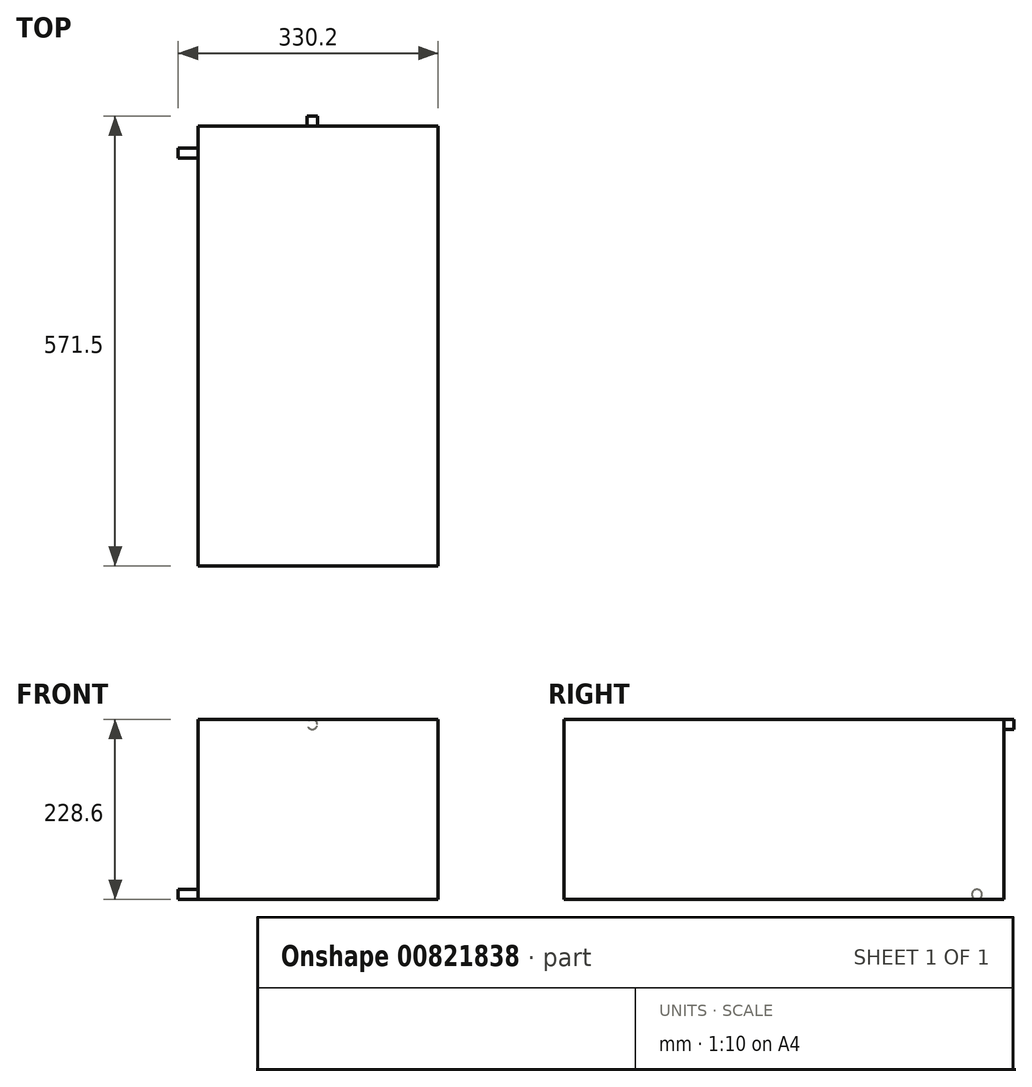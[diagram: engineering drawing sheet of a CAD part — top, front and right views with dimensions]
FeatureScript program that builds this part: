
annotation { "Feature Type Name" : "Feature", "Feature Type Description" : "" }
export const myFeature = defineFeature(function(context is Context, id is Id, definition is map)
    precondition{}
    {
        {
            var Q0;
            Q0=qCreatedBy(makeId("Top.planeOp"),FACE);
            var sketch = newSketch(context, id + "F0", { "sketchPlane" : qUnion([Q0])});
            skLineSegment(sketch, "E0", {"start": v(0, 0) * mm, "end": v(-304.8, 0) * mm});
            skLineSegment(sketch, "E1", {"start": v(0, 0) * mm, "end": v(0, 558.8) * mm});
            skLineSegment(sketch, "E2", {"start": v(0, 558.8) * mm, "end": v(-304.8, 558.8) * mm});
            skLineSegment(sketch, "E3", {"start": v(-304.8, 558.8) * mm, "end": v(-304.8, 0) * mm});
            skSolve(sketch);
        }
        {
            var Q0;
            Q0 = qSketchRegion(id + "F0", true);
            extrude(context, id + "F1", {"entities" : qUnion([Q0]), "depth" : 228.6 * mm, "offsetDistance" : 25.4 * mm});
        }
        {
            var Q0;
            Q0=makeQuery(id+"F1.opExtrude","SWEPT_FACE",FACE,{"disambiguationData":[OSD([sQuery(id+"F0.wireOp",EDGE,"E3")])]});
            var sketch = newSketch(context, id + "F2", { "sketchPlane" : qUnion([Q0])});
            skCircle(sketch, "E4", {"center": v(-524.49, 6.35) * mm, "radius": 6.35 * mm});
            skSolve(sketch);
        }
        {
            var Q0;
            Q0 = qSketchRegion(id + "F2", true);
            extrude(context, id + "F3", {"entities" : qUnion([Q0]), "operationType" : NewBodyOperationType.ADD, "depth" : 25.4 * mm, "offsetDistance" : 25.4 * mm});
        }
        {
            var Q0;
            Q0=makeQuery(id+"F1.opExtrude","SWEPT_FACE",FACE,{"disambiguationData":[OSD([sQuery(id+"F0.wireOp",EDGE,"E2")])]});
            var sketch = newSketch(context, id + "F4", { "sketchPlane" : qUnion([Q0])});
            skCircle(sketch, "E5", {"center": v(159.86, 222.25) * mm, "radius": 6.35 * mm});
            skSolve(sketch);
        }
        {
            var Q0;
            Q0 = qSketchRegion(id + "F4", true);
            extrude(context, id + "F5", {"entities" : qUnion([Q0]), "depth" : 12.7 * mm, "offsetDistance" : 25.4 * mm});
        }
    });
